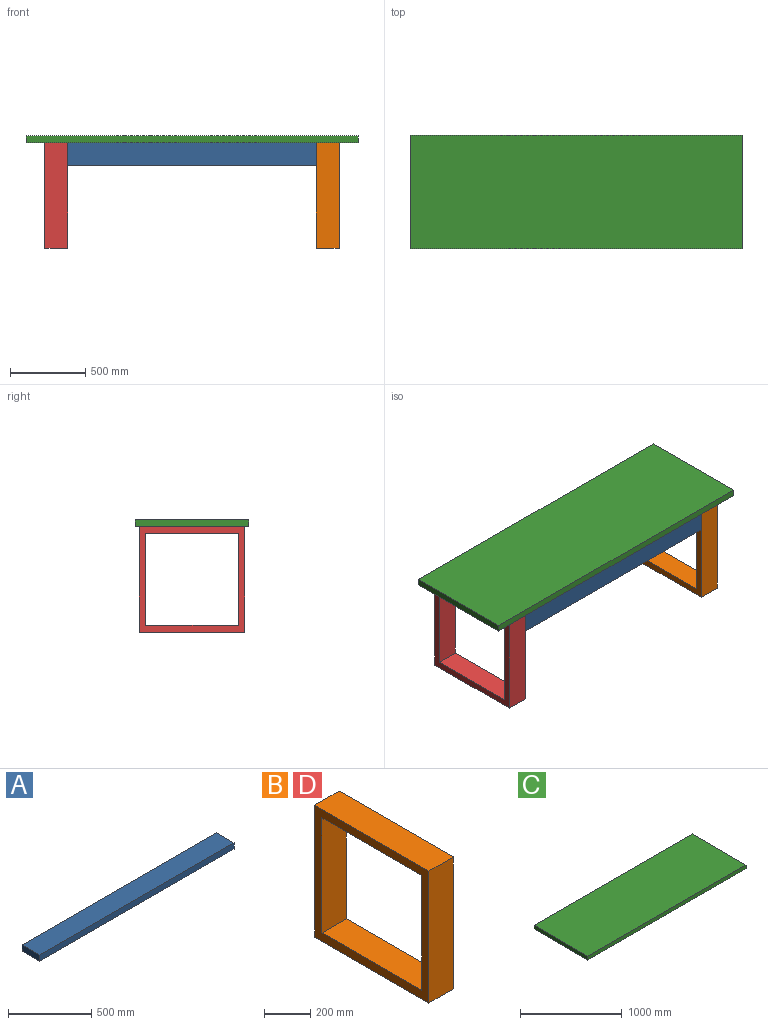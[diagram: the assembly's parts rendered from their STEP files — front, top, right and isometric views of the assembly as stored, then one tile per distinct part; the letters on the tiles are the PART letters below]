
ASSEMBLY  parts=4 mates=3
PART A: 6 faces, bbox 1650x150x45 mm
  f0: plane 1650x45mm, normal (0,-1,0), area 74250mm2, adj f1,f3,f4,f5
  f1: plane 1650x150mm, normal (0,0,-1), area 247500mm2, adj f0,f2,f4,f5
  f2: plane 1650x45mm, normal (0,1,0), area 74250mm2, adj f1,f3,f4,f5
  f3: plane 1650x150mm, normal (0,0,1), area 247500mm2, adj f0,f2,f4,f5
  f4: plane 150x45mm, normal (1,0,0), area 6750mm2, adj f0,f1,f2,f3
  f5: plane 150x45mm, normal (-1,0,0), area 6750mm2, adj f0,f1,f2,f3
PART B: 10 faces, bbox 150x700x700 mm
  f0: plane 610x150mm, normal (0,0,1), area 91500mm2, adj f1,f7,f8,f9
  f1: plane 610x150mm, normal (0,1,0), area 91500mm2, adj f0,f2,f8,f9
  f2: plane 610x150mm, normal (0,0,-1), area 91500mm2, adj f1,f7,f8,f9
  f3: plane 700x150mm, normal (0,-1,0), area 105000mm2, adj f4,f6,f8,f9
  f4: plane 700x150mm, normal (0,0,-1), area 105000mm2, adj f3,f5,f8,f9
  f5: plane 700x150mm, normal (0,1,0), area 105000mm2, adj f4,f6,f8,f9
  f6: plane 700x150mm, normal (0,0,1), area 105000mm2, adj f3,f5,f8,f9
  f7: plane 610x150mm, normal (0,-1,0), area 91500mm2, adj f0,f2,f8,f9
  f8: plane 700x700mm, normal (-1,0,0), area 117900mm2, adj f0,f1,f2,f3,f4,f5,f6,f7
  f9: plane 700x700mm, normal (1,0,0), area 117900mm2, adj f0,f1,f2,f3,f4,f5,f6,f7
PART C: 6 faces, bbox 2200x750x45 mm
  f0: plane 750x45mm, normal (-1,0,0), area 33750mm2, adj f1,f3,f4,f5
  f1: plane 2200x750mm, normal (0,0,-1), area 1650000mm2, adj f0,f2,f4,f5
  f2: plane 750x45mm, normal (1,0,0), area 33750mm2, adj f1,f3,f4,f5
  f3: plane 2200x750mm, normal (0,0,1), area 1650000mm2, adj f0,f2,f4,f5
  f4: plane 2200x45mm, normal (0,1,0), area 99000mm2, adj f0,f1,f2,f3
  f5: plane 2200x45mm, normal (0,-1,0), area 99000mm2, adj f0,f1,f2,f3
PART D: same geometry as B
PLACE A rot(axis=(-1,0,0),90deg) t=(275,25,0)mm
PLACE B t=(2075,25,-700)mm
PLACE C at identity
PLACE D t=(275,25,-700)mm
MATE fastened A.f0 <-> C.f1  axis (0,0,1) through (1100,47.5,0)mm
MATE fastened B.f6 <-> C.f1  axis (0,0,1) through (2000,375,0)mm
MATE fastened D.f6 <-> C.f1  axis (0,0,1) through (200,375,0)mm
